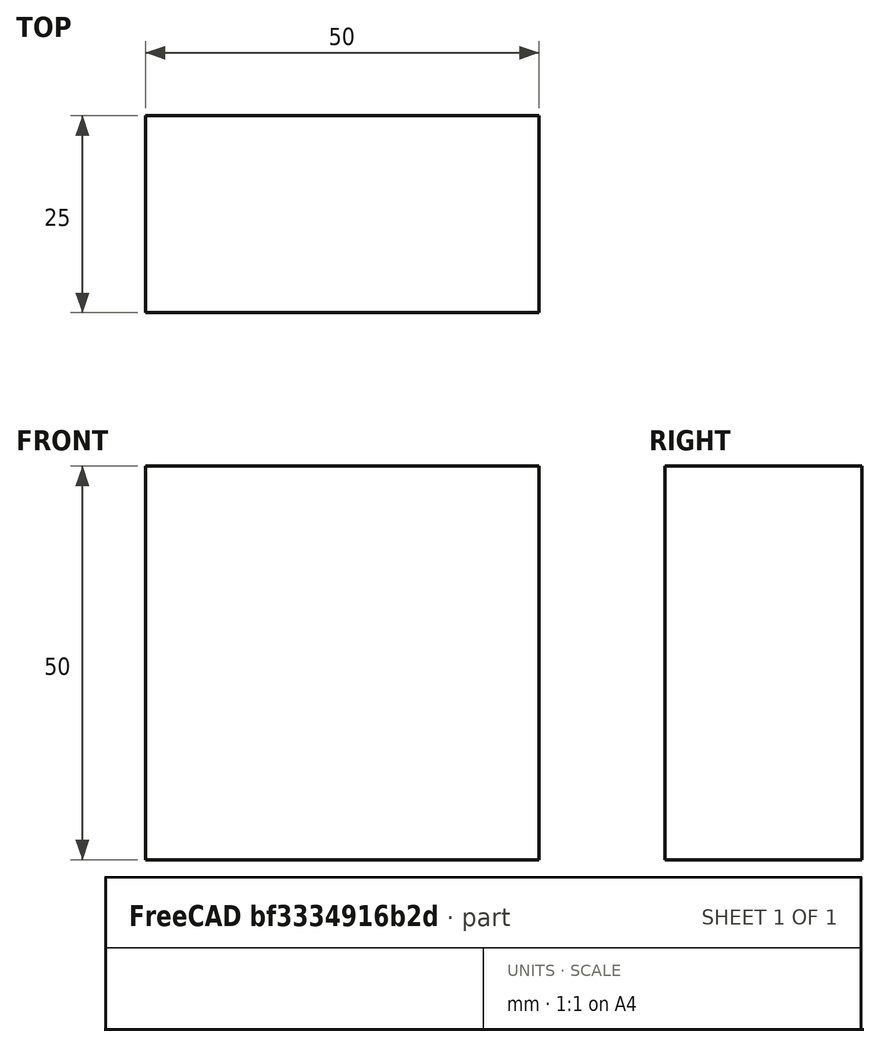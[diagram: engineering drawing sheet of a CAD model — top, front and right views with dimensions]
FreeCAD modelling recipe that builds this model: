
FCSTD DOCUMENT  (FreeCAD 0.15R4671 (Git))
Label: Flat Bar 50x25 EN10058 S235JR
License: All rights reserved
LicenseURL: http://en.wikipedia.org/wiki/All_rights_reserved
objects: Sketcher::SketchObject×1, Part::Extrusion×1
note: 2 computed .brp shape members not serialized (recipe doc carries the construction recipe); baked Part::Feature solids carry a one-line shape summary decoded from their .brp

FEATURE [Sketcher::SketchObject] Sketch
  sketch-geometry (4):
    g0: LineSegment StartX=-25 StartY=-12.5 StartZ=0 EndX=25 EndY=-12.5 EndZ=0
    g1: LineSegment StartX=25 StartY=-12.5 StartZ=0 EndX=25 EndY=12.5 EndZ=0
    g2: LineSegment StartX=25 StartY=12.5 StartZ=0 EndX=-25 EndY=12.5 EndZ=0
    g3: LineSegment StartX=-25 StartY=12.5 StartZ=0 EndX=-25 EndY=-12.5 EndZ=0
  constraints (12):
    c: Coincident(g0,g1)
    c: Coincident(g1,g2)
    c: Coincident(g2,g3)
    c: Coincident(g3,g0)
    c: Horizontal(g0)
    c: Horizontal(g2)
    c: Vertical(g1)
    c: Vertical(g3)
    c: Symmetric(g1,g2,g-2)
    c: Symmetric(g0,g1,g-1)
    c: DistanceY(g1) = 25
    c: DistanceX(g0) = 50
FEATURE [Part::Extrusion] Extrude  label="Flat Bar 50x25 EN10058 S235JR"
  Base = -> Sketch
  Dir = (0,0,50)
  Solid = true
